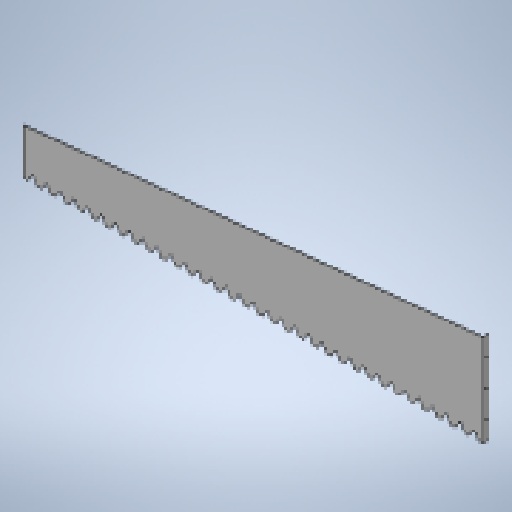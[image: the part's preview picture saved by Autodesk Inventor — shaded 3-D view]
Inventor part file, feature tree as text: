
AUTODESK INVENTOR PART (.ipt)
format: ipt  version: 2025 (Build 290162010, 162A)  size: 697,344 bytes
history: native  units: mm
features: other x5, sketch x2
ambient origin geometry x8: Origin, YZ Plane, XZ Plane, XY Plane, X Axis, Y Axis, Z Axis, Center Point
bodies: Solid1 (feature_tree)
feature tree (7):
  other  "MSC 706 ridge 1.ipt"
  other  "A-Side Definition"
  other  "Solid1::MSC 706 ridge 1.ipt"
  other  "TaggingFeature1"
  sketch  "Sketch1"  dims[d0=10.0mm]
  sketch  "Sketch4"  dims[d1=2.0mm]
  other  "Definition1"
